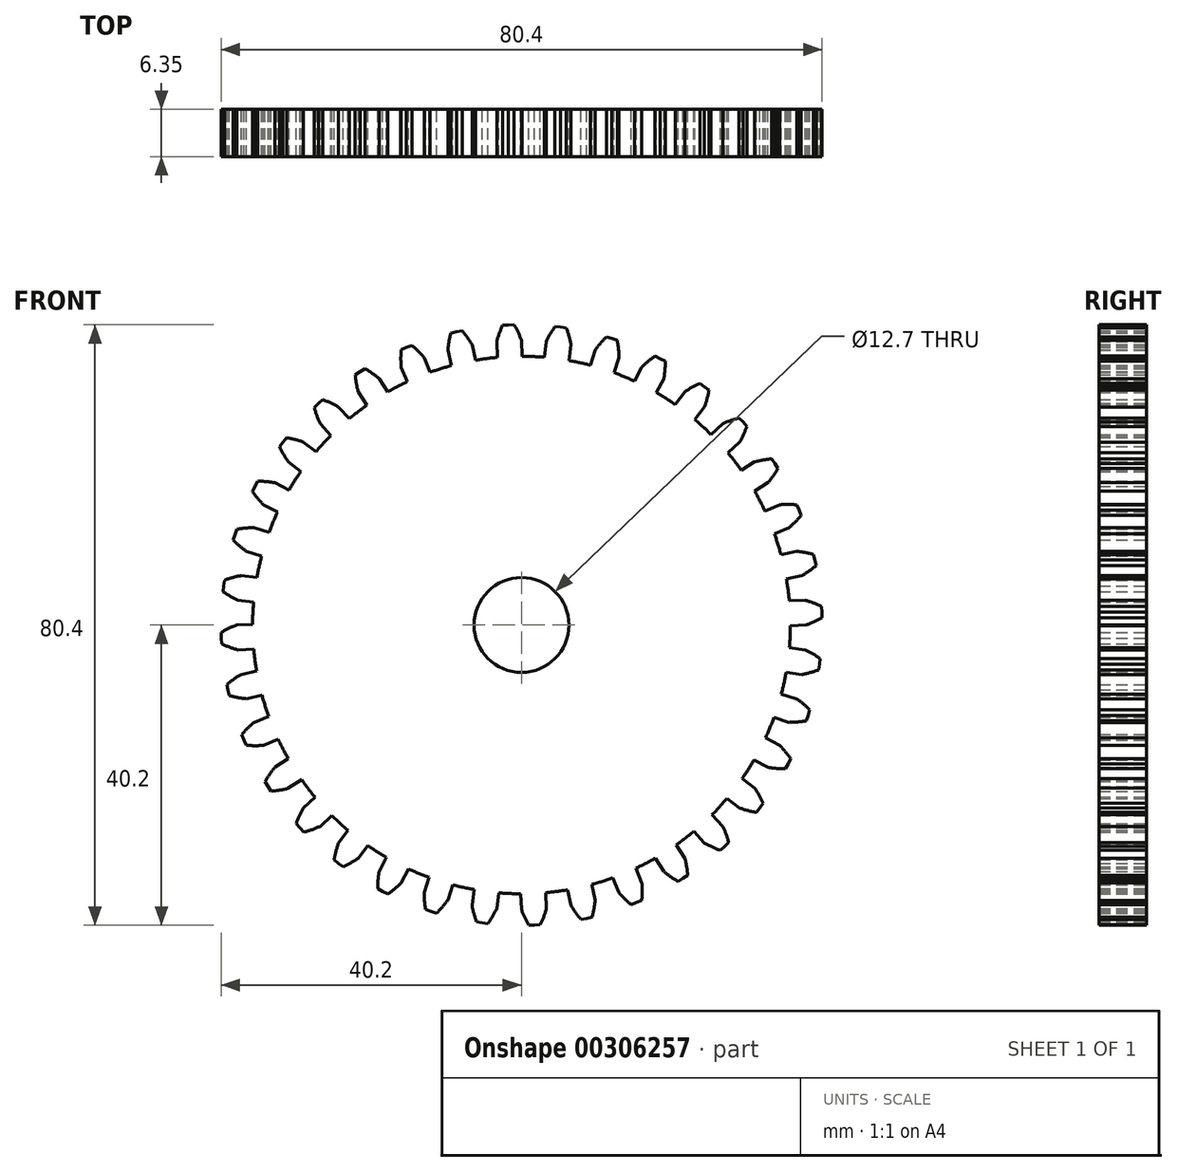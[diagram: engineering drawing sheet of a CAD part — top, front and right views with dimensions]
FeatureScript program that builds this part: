
annotation { "Feature Type Name" : "Feature", "Feature Type Description" : "" }
export const myFeature = defineFeature(function(context is Context, id is Id, definition is map)
    precondition{}
    {
        {
            var Q0;
            Q0=qCreatedBy(makeId("Front.planeOp"),FACE);
            var sketch = newSketch(context, id + "F0", { "sketchPlane" : qUnion([Q0])});
            skArc(sketch, "E0", {"start": v(-3.23, 35.83) * mm, "mid": v(1.57, -35.94) * mm, "end": v(0.1, 35.98) * mm});
            skArc(sketch, "E1.trimOffspring", {"start": v(0, 38.1) * mm, "mid": v(-0.45, 39.17) * mm, "end": v(-0.99, 40.2) * mm});
            skLineSegment(sketch, "E2", {"start": v(0, 38.1) * mm, "end": v(0.1, 35.98) * mm});
            skLineSegment(sketch, "E3", {"start": v(-0.99, 40.2) * mm, "end": v(-1.75, 40.18) * mm});
            skLineSegment(sketch, "E4.MirrorCS", {"start": v(-2.52, 40.13) * mm, "end": v(-1.75, 40.18) * mm});
            skArc(sketch, "E5.MirrorCS", {"start": v(-3.32, 37.95) * mm, "mid": v(-2.97, 39.06) * mm, "end": v(-2.52, 40.13) * mm});
            skLineSegment(sketch, "E6.MirrorCS", {"start": v(-3.32, 37.95) * mm, "end": v(-3.23, 35.83) * mm});
            skPoint(sketch, "E7.orphan", {"position": v(-3.18, 34.7) * mm});
            skPoint(sketch, "E8.orphan", {"position": v(0.14, 34.85) * mm});
            skLineSegment(sketch, "E9.1.0", {"start": v(-31.2, -21.85) * mm, "end": v(-29.42, -20.71) * mm});
            skLineSegment(sketch, "E9.2.0", {"start": v(34.53, -16.1) * mm, "end": v(32.65, -15.12) * mm});
            skLineSegment(sketch, "E10.1.0", {"start": v(-9.86, 36.8) * mm, "end": v(-9.4, 34.73) * mm});
            skArc(sketch, "E10.1.1", {"start": v(-9.86, 36.8) * mm, "mid": v(-9.7, 37.95) * mm, "end": v(-9.45, 39.08) * mm});
            skLineSegment(sketch, "E10.1.2", {"start": v(-9.45, 39.08) * mm, "end": v(-8.7, 39.26) * mm});
            skLineSegment(sketch, "E10.1.3", {"start": v(-7.95, 39.41) * mm, "end": v(-8.7, 39.26) * mm});
            skArc(sketch, "E10.1.4", {"start": v(-6.62, 37.52) * mm, "mid": v(-7.24, 38.5) * mm, "end": v(-7.95, 39.41) * mm});
            skLineSegment(sketch, "E10.1.5", {"start": v(-6.62, 37.52) * mm, "end": v(-6.16, 35.45) * mm});
            skLineSegment(sketch, "E10.2.0", {"start": v(-16.1, 34.53) * mm, "end": v(-15.29, 32.57) * mm});
            skArc(sketch, "E10.2.1", {"start": v(-16.1, 34.53) * mm, "mid": v(-16.15, 35.69) * mm, "end": v(-16.1, 36.85) * mm});
            skLineSegment(sketch, "E10.2.2", {"start": v(-16.1, 36.85) * mm, "end": v(-15.39, 37.15) * mm});
            skLineSegment(sketch, "E10.2.3", {"start": v(-14.68, 37.43) * mm, "end": v(-15.39, 37.15) * mm});
            skArc(sketch, "E10.2.4", {"start": v(-13.03, 35.8) * mm, "mid": v(-13.82, 36.66) * mm, "end": v(-14.68, 37.43) * mm});
            skLineSegment(sketch, "E10.2.5", {"start": v(-13.03, 35.8) * mm, "end": v(-12.22, 33.84) * mm});
            skLineSegment(sketch, "E10.3.0", {"start": v(-21.85, 31.2) * mm, "end": v(-20.71, 29.42) * mm});
            skArc(sketch, "E10.3.1", {"start": v(-21.85, 31.2) * mm, "mid": v(-22.1, 32.34) * mm, "end": v(-22.25, 33.5) * mm});
            skLineSegment(sketch, "E10.3.2", {"start": v(-22.25, 33.5) * mm, "end": v(-21.6, 33.92) * mm});
            skLineSegment(sketch, "E10.3.3", {"start": v(-20.95, 34.32) * mm, "end": v(-21.6, 33.92) * mm});
            skArc(sketch, "E10.3.4", {"start": v(-19.05, 33) * mm, "mid": v(-19.97, 33.7) * mm, "end": v(-20.95, 34.32) * mm});
            skLineSegment(sketch, "E10.3.5", {"start": v(-19.05, 33) * mm, "end": v(-17.9, 31.2) * mm});
            skLineSegment(sketch, "E10.4.0", {"start": v(-26.94, 26.94) * mm, "end": v(-25.5, 25.38) * mm});
            skArc(sketch, "E10.4.1", {"start": v(-26.94, 26.94) * mm, "mid": v(-27.38, 28.01) * mm, "end": v(-27.72, 29.12) * mm});
            skLineSegment(sketch, "E10.4.2", {"start": v(-27.72, 29.12) * mm, "end": v(-27.17, 29.65) * mm});
            skLineSegment(sketch, "E10.4.3", {"start": v(-26.6, 30.16) * mm, "end": v(-27.17, 29.65) * mm});
            skArc(sketch, "E10.4.4", {"start": v(-24.5, 29.19) * mm, "mid": v(-25.52, 29.72) * mm, "end": v(-26.6, 30.16) * mm});
            skLineSegment(sketch, "E10.4.5", {"start": v(-24.5, 29.19) * mm, "end": v(-23.06, 27.62) * mm});
            skLineSegment(sketch, "E10.5.0", {"start": v(-31.2, 21.85) * mm, "end": v(-29.53, 20.56) * mm});
            skArc(sketch, "E10.5.1", {"start": v(-31.2, 21.85) * mm, "mid": v(-31.83, 22.83) * mm, "end": v(-32.36, 23.87) * mm});
            skLineSegment(sketch, "E10.5.2", {"start": v(-32.36, 23.87) * mm, "end": v(-31.9, 24.48) * mm});
            skLineSegment(sketch, "E10.5.3", {"start": v(-31.43, 25.08) * mm, "end": v(-31.9, 24.48) * mm});
            skArc(sketch, "E10.5.4", {"start": v(-29.19, 24.5) * mm, "mid": v(-30.3, 24.84) * mm, "end": v(-31.43, 25.08) * mm});
            skLineSegment(sketch, "E10.5.5", {"start": v(-29.19, 24.5) * mm, "end": v(-27.5, 23.2) * mm});
            skLineSegment(sketch, "E10.6.0", {"start": v(-34.53, 16.1) * mm, "end": v(-32.65, 15.12) * mm});
            skArc(sketch, "E10.6.1", {"start": v(-34.53, 16.1) * mm, "mid": v(-35.31, 16.96) * mm, "end": v(-36.01, 17.88) * mm});
            skLineSegment(sketch, "E10.6.2", {"start": v(-36.01, 17.88) * mm, "end": v(-35.67, 18.57) * mm});
            skLineSegment(sketch, "E10.6.3", {"start": v(-35.3, 19.24) * mm, "end": v(-35.67, 18.57) * mm});
            skArc(sketch, "E10.6.4", {"start": v(-33, 19.05) * mm, "mid": v(-34.15, 19.2) * mm, "end": v(-35.3, 19.24) * mm});
            skLineSegment(sketch, "E10.6.5", {"start": v(-33, 19.05) * mm, "end": v(-31.11, 18.07) * mm});
            skLineSegment(sketch, "E10.7.0", {"start": v(-36.8, 9.86) * mm, "end": v(-34.78, 9.22) * mm});
            skArc(sketch, "E10.7.1", {"start": v(-36.8, 9.86) * mm, "mid": v(-37.72, 10.57) * mm, "end": v(-38.57, 11.36) * mm});
            skLineSegment(sketch, "E10.7.2", {"start": v(-38.57, 11.36) * mm, "end": v(-38.35, 12.1) * mm});
            skLineSegment(sketch, "E10.7.3", {"start": v(-38.1, 12.82) * mm, "end": v(-38.35, 12.1) * mm});
            skArc(sketch, "E10.7.4", {"start": v(-35.8, 13.03) * mm, "mid": v(-36.96, 12.98) * mm, "end": v(-38.1, 12.82) * mm});
            skLineSegment(sketch, "E10.7.5", {"start": v(-35.8, 13.03) * mm, "end": v(-33.78, 12.4) * mm});
            skLineSegment(sketch, "E10.8.0", {"start": v(-37.95, 3.32) * mm, "end": v(-35.85, 3.04) * mm});
            skArc(sketch, "E10.8.1", {"start": v(-37.95, 3.32) * mm, "mid": v(-38.98, 3.86) * mm, "end": v(-39.96, 4.49) * mm});
            skLineSegment(sketch, "E10.8.2", {"start": v(-39.96, 4.49) * mm, "end": v(-39.87, 5.25) * mm});
            skLineSegment(sketch, "E10.8.3", {"start": v(-39.76, 6) * mm, "end": v(-39.87, 5.25) * mm});
            skArc(sketch, "E10.8.4", {"start": v(-37.52, 6.62) * mm, "mid": v(-38.65, 6.36) * mm, "end": v(-39.76, 6) * mm});
            skLineSegment(sketch, "E10.8.5", {"start": v(-37.52, 6.62) * mm, "end": v(-35.42, 6.34) * mm});
            skLineSegment(sketch, "E10.9.0", {"start": v(-37.95, -3.32) * mm, "end": v(-35.83, -3.23) * mm});
            skArc(sketch, "E10.9.1", {"start": v(-37.95, -3.32) * mm, "mid": v(-39.06, -2.97) * mm, "end": v(-40.13, -2.52) * mm});
            skLineSegment(sketch, "E10.9.2", {"start": v(-40.13, -2.52) * mm, "end": v(-40.18, -1.75) * mm});
            skLineSegment(sketch, "E10.9.3", {"start": v(-40.2, -0.99) * mm, "end": v(-40.18, -1.75) * mm});
            skArc(sketch, "E10.9.4", {"start": v(-38.1, 0) * mm, "mid": v(-39.17, -0.45) * mm, "end": v(-40.2, -0.99) * mm});
            skLineSegment(sketch, "E10.9.5", {"start": v(-38.1, 0) * mm, "end": v(-35.98, 0.1) * mm});
            skLineSegment(sketch, "E10.10.0", {"start": v(-36.8, -9.86) * mm, "end": v(-34.73, -9.4) * mm});
            skArc(sketch, "E10.10.1", {"start": v(-36.8, -9.86) * mm, "mid": v(-37.95, -9.7) * mm, "end": v(-39.08, -9.45) * mm});
            skLineSegment(sketch, "E10.10.2", {"start": v(-39.08, -9.45) * mm, "end": v(-39.26, -8.7) * mm});
            skLineSegment(sketch, "E10.10.3", {"start": v(-39.41, -7.95) * mm, "end": v(-39.26, -8.7) * mm});
            skArc(sketch, "E10.10.4", {"start": v(-37.52, -6.62) * mm, "mid": v(-38.5, -7.24) * mm, "end": v(-39.41, -7.95) * mm});
            skLineSegment(sketch, "E10.10.5", {"start": v(-37.52, -6.62) * mm, "end": v(-35.45, -6.16) * mm});
            skLineSegment(sketch, "E10.11.0", {"start": v(-34.53, -16.1) * mm, "end": v(-32.57, -15.29) * mm});
            skArc(sketch, "E10.11.1", {"start": v(-34.53, -16.1) * mm, "mid": v(-35.69, -16.15) * mm, "end": v(-36.85, -16.1) * mm});
            skLineSegment(sketch, "E10.11.2", {"start": v(-36.85, -16.1) * mm, "end": v(-37.15, -15.39) * mm});
            skLineSegment(sketch, "E10.11.3", {"start": v(-37.43, -14.68) * mm, "end": v(-37.15, -15.39) * mm});
            skArc(sketch, "E10.11.4", {"start": v(-35.8, -13.03) * mm, "mid": v(-36.66, -13.82) * mm, "end": v(-37.43, -14.68) * mm});
            skLineSegment(sketch, "E10.11.5", {"start": v(-35.8, -13.03) * mm, "end": v(-33.84, -12.22) * mm});
            skArc(sketch, "E10.12.1", {"start": v(-31.2, -21.85) * mm, "mid": v(-32.34, -22.1) * mm, "end": v(-33.5, -22.25) * mm});
            skLineSegment(sketch, "E10.12.2", {"start": v(-33.5, -22.25) * mm, "end": v(-33.92, -21.6) * mm});
            skLineSegment(sketch, "E10.12.3", {"start": v(-34.32, -20.95) * mm, "end": v(-33.92, -21.6) * mm});
            skArc(sketch, "E10.12.4", {"start": v(-33, -19.05) * mm, "mid": v(-33.7, -19.97) * mm, "end": v(-34.32, -20.95) * mm});
            skLineSegment(sketch, "E10.12.5", {"start": v(-33, -19.05) * mm, "end": v(-31.2, -17.9) * mm});
            skLineSegment(sketch, "E10.13.0", {"start": v(-26.94, -26.94) * mm, "end": v(-25.38, -25.5) * mm});
            skArc(sketch, "E10.13.1", {"start": v(-26.94, -26.94) * mm, "mid": v(-28.01, -27.38) * mm, "end": v(-29.12, -27.72) * mm});
            skLineSegment(sketch, "E10.13.2", {"start": v(-29.12, -27.72) * mm, "end": v(-29.65, -27.17) * mm});
            skLineSegment(sketch, "E10.13.3", {"start": v(-30.16, -26.6) * mm, "end": v(-29.65, -27.17) * mm});
            skArc(sketch, "E10.13.4", {"start": v(-29.19, -24.5) * mm, "mid": v(-29.72, -25.52) * mm, "end": v(-30.16, -26.6) * mm});
            skLineSegment(sketch, "E10.13.5", {"start": v(-29.19, -24.5) * mm, "end": v(-27.62, -23.06) * mm});
            skLineSegment(sketch, "E10.14.0", {"start": v(-21.85, -31.2) * mm, "end": v(-20.56, -29.53) * mm});
            skArc(sketch, "E10.14.1", {"start": v(-21.85, -31.2) * mm, "mid": v(-22.83, -31.83) * mm, "end": v(-23.87, -32.36) * mm});
            skLineSegment(sketch, "E10.14.2", {"start": v(-23.87, -32.36) * mm, "end": v(-24.48, -31.9) * mm});
            skLineSegment(sketch, "E10.14.3", {"start": v(-25.08, -31.43) * mm, "end": v(-24.48, -31.9) * mm});
            skArc(sketch, "E10.14.4", {"start": v(-24.5, -29.19) * mm, "mid": v(-24.84, -30.3) * mm, "end": v(-25.08, -31.43) * mm});
            skLineSegment(sketch, "E10.14.5", {"start": v(-24.5, -29.19) * mm, "end": v(-23.2, -27.5) * mm});
            skLineSegment(sketch, "E10.15.0", {"start": v(-16.1, -34.53) * mm, "end": v(-15.12, -32.65) * mm});
            skArc(sketch, "E10.15.1", {"start": v(-16.1, -34.53) * mm, "mid": v(-16.96, -35.31) * mm, "end": v(-17.88, -36.01) * mm});
            skLineSegment(sketch, "E10.15.2", {"start": v(-17.88, -36.01) * mm, "end": v(-18.57, -35.67) * mm});
            skLineSegment(sketch, "E10.15.3", {"start": v(-19.24, -35.3) * mm, "end": v(-18.57, -35.67) * mm});
            skArc(sketch, "E10.15.4", {"start": v(-19.05, -33) * mm, "mid": v(-19.2, -34.15) * mm, "end": v(-19.24, -35.3) * mm});
            skLineSegment(sketch, "E10.15.5", {"start": v(-19.05, -33) * mm, "end": v(-18.07, -31.11) * mm});
            skLineSegment(sketch, "E10.16.0", {"start": v(-9.86, -36.8) * mm, "end": v(-9.22, -34.78) * mm});
            skArc(sketch, "E10.16.1", {"start": v(-9.86, -36.8) * mm, "mid": v(-10.57, -37.72) * mm, "end": v(-11.36, -38.57) * mm});
            skLineSegment(sketch, "E10.16.2", {"start": v(-11.36, -38.57) * mm, "end": v(-12.1, -38.35) * mm});
            skLineSegment(sketch, "E10.16.3", {"start": v(-12.82, -38.1) * mm, "end": v(-12.1, -38.35) * mm});
            skArc(sketch, "E10.16.4", {"start": v(-13.03, -35.8) * mm, "mid": v(-12.98, -36.96) * mm, "end": v(-12.82, -38.1) * mm});
            skLineSegment(sketch, "E10.16.5", {"start": v(-13.03, -35.8) * mm, "end": v(-12.4, -33.78) * mm});
            skLineSegment(sketch, "E10.17.0", {"start": v(-3.32, -37.95) * mm, "end": v(-3.04, -35.85) * mm});
            skArc(sketch, "E10.17.1", {"start": v(-3.32, -37.95) * mm, "mid": v(-3.86, -38.98) * mm, "end": v(-4.49, -39.96) * mm});
            skLineSegment(sketch, "E10.17.2", {"start": v(-4.49, -39.96) * mm, "end": v(-5.25, -39.87) * mm});
            skLineSegment(sketch, "E10.17.3", {"start": v(-6, -39.76) * mm, "end": v(-5.25, -39.87) * mm});
            skArc(sketch, "E10.17.4", {"start": v(-6.62, -37.52) * mm, "mid": v(-6.36, -38.65) * mm, "end": v(-6, -39.76) * mm});
            skLineSegment(sketch, "E10.17.5", {"start": v(-6.62, -37.52) * mm, "end": v(-6.34, -35.42) * mm});
            skLineSegment(sketch, "E10.18.0", {"start": v(3.32, -37.95) * mm, "end": v(3.23, -35.83) * mm});
            skArc(sketch, "E10.18.1", {"start": v(3.32, -37.95) * mm, "mid": v(2.97, -39.06) * mm, "end": v(2.52, -40.13) * mm});
            skLineSegment(sketch, "E10.18.2", {"start": v(2.52, -40.13) * mm, "end": v(1.75, -40.18) * mm});
            skLineSegment(sketch, "E10.18.3", {"start": v(0.99, -40.2) * mm, "end": v(1.75, -40.18) * mm});
            skArc(sketch, "E10.18.4", {"start": v(0, -38.1) * mm, "mid": v(0.45, -39.17) * mm, "end": v(0.99, -40.2) * mm});
            skLineSegment(sketch, "E10.18.5", {"start": v(0, -38.1) * mm, "end": v(-0.1, -35.98) * mm});
            skLineSegment(sketch, "E10.19.0", {"start": v(9.86, -36.8) * mm, "end": v(9.4, -34.73) * mm});
            skArc(sketch, "E10.19.1", {"start": v(9.86, -36.8) * mm, "mid": v(9.7, -37.95) * mm, "end": v(9.45, -39.08) * mm});
            skLineSegment(sketch, "E10.19.2", {"start": v(9.45, -39.08) * mm, "end": v(8.7, -39.26) * mm});
            skLineSegment(sketch, "E10.19.3", {"start": v(7.95, -39.41) * mm, "end": v(8.7, -39.26) * mm});
            skArc(sketch, "E10.19.4", {"start": v(6.62, -37.52) * mm, "mid": v(7.24, -38.5) * mm, "end": v(7.95, -39.41) * mm});
            skLineSegment(sketch, "E10.19.5", {"start": v(6.62, -37.52) * mm, "end": v(6.16, -35.45) * mm});
            skLineSegment(sketch, "E10.20.0", {"start": v(16.1, -34.53) * mm, "end": v(15.29, -32.57) * mm});
            skArc(sketch, "E10.20.1", {"start": v(16.1, -34.53) * mm, "mid": v(16.15, -35.69) * mm, "end": v(16.1, -36.85) * mm});
            skLineSegment(sketch, "E10.20.2", {"start": v(16.1, -36.85) * mm, "end": v(15.39, -37.15) * mm});
            skLineSegment(sketch, "E10.20.3", {"start": v(14.68, -37.43) * mm, "end": v(15.39, -37.15) * mm});
            skArc(sketch, "E10.20.4", {"start": v(13.03, -35.8) * mm, "mid": v(13.82, -36.66) * mm, "end": v(14.68, -37.43) * mm});
            skLineSegment(sketch, "E10.20.5", {"start": v(13.03, -35.8) * mm, "end": v(12.22, -33.84) * mm});
            skLineSegment(sketch, "E10.21.0", {"start": v(21.85, -31.2) * mm, "end": v(20.71, -29.42) * mm});
            skArc(sketch, "E10.21.1", {"start": v(21.85, -31.2) * mm, "mid": v(22.1, -32.34) * mm, "end": v(22.25, -33.5) * mm});
            skLineSegment(sketch, "E10.21.2", {"start": v(22.25, -33.5) * mm, "end": v(21.6, -33.92) * mm});
            skLineSegment(sketch, "E10.21.3", {"start": v(20.95, -34.32) * mm, "end": v(21.6, -33.92) * mm});
            skArc(sketch, "E10.21.4", {"start": v(19.05, -33) * mm, "mid": v(19.97, -33.7) * mm, "end": v(20.95, -34.32) * mm});
            skLineSegment(sketch, "E10.21.5", {"start": v(19.05, -33) * mm, "end": v(17.9, -31.2) * mm});
            skLineSegment(sketch, "E10.22.0", {"start": v(26.94, -26.94) * mm, "end": v(25.5, -25.38) * mm});
            skArc(sketch, "E10.22.1", {"start": v(26.94, -26.94) * mm, "mid": v(27.38, -28.01) * mm, "end": v(27.72, -29.12) * mm});
            skLineSegment(sketch, "E10.22.2", {"start": v(27.72, -29.12) * mm, "end": v(27.17, -29.65) * mm});
            skLineSegment(sketch, "E10.22.3", {"start": v(26.6, -30.16) * mm, "end": v(27.17, -29.65) * mm});
            skArc(sketch, "E10.22.4", {"start": v(24.5, -29.19) * mm, "mid": v(25.52, -29.72) * mm, "end": v(26.6, -30.16) * mm});
            skLineSegment(sketch, "E10.22.5", {"start": v(24.5, -29.19) * mm, "end": v(23.06, -27.62) * mm});
            skLineSegment(sketch, "E10.23.0", {"start": v(31.2, -21.85) * mm, "end": v(29.53, -20.56) * mm});
            skArc(sketch, "E10.23.1", {"start": v(31.2, -21.85) * mm, "mid": v(31.83, -22.83) * mm, "end": v(32.36, -23.87) * mm});
            skLineSegment(sketch, "E10.23.2", {"start": v(32.36, -23.87) * mm, "end": v(31.9, -24.48) * mm});
            skLineSegment(sketch, "E10.23.3", {"start": v(31.43, -25.08) * mm, "end": v(31.9, -24.48) * mm});
            skArc(sketch, "E10.23.4", {"start": v(29.19, -24.5) * mm, "mid": v(30.3, -24.84) * mm, "end": v(31.43, -25.08) * mm});
            skLineSegment(sketch, "E10.23.5", {"start": v(29.19, -24.5) * mm, "end": v(27.5, -23.2) * mm});
            skArc(sketch, "E10.24.1", {"start": v(34.53, -16.1) * mm, "mid": v(35.31, -16.96) * mm, "end": v(36.01, -17.88) * mm});
            skLineSegment(sketch, "E10.24.2", {"start": v(36.01, -17.88) * mm, "end": v(35.67, -18.57) * mm});
            skLineSegment(sketch, "E10.24.3", {"start": v(35.3, -19.24) * mm, "end": v(35.67, -18.57) * mm});
            skArc(sketch, "E10.24.4", {"start": v(33, -19.05) * mm, "mid": v(34.15, -19.2) * mm, "end": v(35.3, -19.24) * mm});
            skLineSegment(sketch, "E10.24.5", {"start": v(33, -19.05) * mm, "end": v(31.11, -18.07) * mm});
            skLineSegment(sketch, "E10.25.0", {"start": v(36.8, -9.86) * mm, "end": v(34.78, -9.22) * mm});
            skArc(sketch, "E10.25.1", {"start": v(36.8, -9.86) * mm, "mid": v(37.72, -10.57) * mm, "end": v(38.57, -11.36) * mm});
            skLineSegment(sketch, "E10.25.2", {"start": v(38.57, -11.36) * mm, "end": v(38.35, -12.1) * mm});
            skLineSegment(sketch, "E10.25.3", {"start": v(38.1, -12.82) * mm, "end": v(38.35, -12.1) * mm});
            skArc(sketch, "E10.25.4", {"start": v(35.8, -13.03) * mm, "mid": v(36.96, -12.98) * mm, "end": v(38.1, -12.82) * mm});
            skLineSegment(sketch, "E10.25.5", {"start": v(35.8, -13.03) * mm, "end": v(33.78, -12.4) * mm});
            skLineSegment(sketch, "E10.26.0", {"start": v(37.95, -3.32) * mm, "end": v(35.85, -3.04) * mm});
            skArc(sketch, "E10.26.1", {"start": v(37.95, -3.32) * mm, "mid": v(38.98, -3.86) * mm, "end": v(39.96, -4.49) * mm});
            skLineSegment(sketch, "E10.26.2", {"start": v(39.96, -4.49) * mm, "end": v(39.87, -5.25) * mm});
            skLineSegment(sketch, "E10.26.3", {"start": v(39.76, -6) * mm, "end": v(39.87, -5.25) * mm});
            skArc(sketch, "E10.26.4", {"start": v(37.52, -6.62) * mm, "mid": v(38.65, -6.36) * mm, "end": v(39.76, -6) * mm});
            skLineSegment(sketch, "E10.26.5", {"start": v(37.52, -6.62) * mm, "end": v(35.42, -6.34) * mm});
            skLineSegment(sketch, "E10.27.0", {"start": v(37.95, 3.32) * mm, "end": v(35.83, 3.23) * mm});
            skArc(sketch, "E10.27.1", {"start": v(37.95, 3.32) * mm, "mid": v(39.06, 2.97) * mm, "end": v(40.13, 2.52) * mm});
            skLineSegment(sketch, "E10.27.2", {"start": v(40.13, 2.52) * mm, "end": v(40.18, 1.75) * mm});
            skLineSegment(sketch, "E10.27.3", {"start": v(40.2, 0.99) * mm, "end": v(40.18, 1.75) * mm});
            skArc(sketch, "E10.27.4", {"start": v(38.1, 0) * mm, "mid": v(39.17, 0.45) * mm, "end": v(40.2, 0.99) * mm});
            skLineSegment(sketch, "E10.27.5", {"start": v(38.1, 0) * mm, "end": v(35.98, -0.1) * mm});
            skLineSegment(sketch, "E10.28.0", {"start": v(36.8, 9.86) * mm, "end": v(34.73, 9.4) * mm});
            skArc(sketch, "E10.28.1", {"start": v(36.8, 9.86) * mm, "mid": v(37.95, 9.7) * mm, "end": v(39.08, 9.45) * mm});
            skLineSegment(sketch, "E10.28.2", {"start": v(39.08, 9.45) * mm, "end": v(39.26, 8.7) * mm});
            skLineSegment(sketch, "E10.28.3", {"start": v(39.41, 7.95) * mm, "end": v(39.26, 8.7) * mm});
            skArc(sketch, "E10.28.4", {"start": v(37.52, 6.62) * mm, "mid": v(38.5, 7.24) * mm, "end": v(39.41, 7.95) * mm});
            skLineSegment(sketch, "E10.28.5", {"start": v(37.52, 6.62) * mm, "end": v(35.45, 6.16) * mm});
            skLineSegment(sketch, "E10.29.0", {"start": v(34.53, 16.1) * mm, "end": v(32.57, 15.29) * mm});
            skArc(sketch, "E10.29.1", {"start": v(34.53, 16.1) * mm, "mid": v(35.69, 16.15) * mm, "end": v(36.85, 16.1) * mm});
            skLineSegment(sketch, "E10.29.2", {"start": v(36.85, 16.1) * mm, "end": v(37.15, 15.39) * mm});
            skLineSegment(sketch, "E10.29.3", {"start": v(37.43, 14.68) * mm, "end": v(37.15, 15.39) * mm});
            skArc(sketch, "E10.29.4", {"start": v(35.8, 13.03) * mm, "mid": v(36.66, 13.82) * mm, "end": v(37.43, 14.68) * mm});
            skLineSegment(sketch, "E10.29.5", {"start": v(35.8, 13.03) * mm, "end": v(33.84, 12.22) * mm});
            skLineSegment(sketch, "E10.30.0", {"start": v(31.2, 21.85) * mm, "end": v(29.42, 20.71) * mm});
            skArc(sketch, "E10.30.1", {"start": v(31.2, 21.85) * mm, "mid": v(32.34, 22.1) * mm, "end": v(33.5, 22.25) * mm});
            skLineSegment(sketch, "E10.30.2", {"start": v(33.5, 22.25) * mm, "end": v(33.92, 21.6) * mm});
            skLineSegment(sketch, "E10.30.3", {"start": v(34.32, 20.95) * mm, "end": v(33.92, 21.6) * mm});
            skArc(sketch, "E10.30.4", {"start": v(33, 19.05) * mm, "mid": v(33.7, 19.97) * mm, "end": v(34.32, 20.95) * mm});
            skLineSegment(sketch, "E10.30.5", {"start": v(33, 19.05) * mm, "end": v(31.2, 17.9) * mm});
            skLineSegment(sketch, "E10.31.0", {"start": v(26.94, 26.94) * mm, "end": v(25.38, 25.5) * mm});
            skArc(sketch, "E10.31.1", {"start": v(26.94, 26.94) * mm, "mid": v(28.01, 27.38) * mm, "end": v(29.12, 27.72) * mm});
            skLineSegment(sketch, "E10.31.2", {"start": v(29.12, 27.72) * mm, "end": v(29.65, 27.17) * mm});
            skLineSegment(sketch, "E10.31.3", {"start": v(30.16, 26.6) * mm, "end": v(29.65, 27.17) * mm});
            skArc(sketch, "E10.31.4", {"start": v(29.19, 24.5) * mm, "mid": v(29.72, 25.52) * mm, "end": v(30.16, 26.6) * mm});
            skLineSegment(sketch, "E10.31.5", {"start": v(29.19, 24.5) * mm, "end": v(27.62, 23.06) * mm});
            skLineSegment(sketch, "E10.32.0", {"start": v(21.85, 31.2) * mm, "end": v(20.56, 29.53) * mm});
            skArc(sketch, "E10.32.1", {"start": v(21.85, 31.2) * mm, "mid": v(22.83, 31.83) * mm, "end": v(23.87, 32.36) * mm});
            skLineSegment(sketch, "E10.32.2", {"start": v(23.87, 32.36) * mm, "end": v(24.48, 31.9) * mm});
            skLineSegment(sketch, "E10.32.3", {"start": v(25.08, 31.43) * mm, "end": v(24.48, 31.9) * mm});
            skArc(sketch, "E10.32.4", {"start": v(24.5, 29.19) * mm, "mid": v(24.84, 30.3) * mm, "end": v(25.08, 31.43) * mm});
            skLineSegment(sketch, "E10.32.5", {"start": v(24.5, 29.19) * mm, "end": v(23.2, 27.5) * mm});
            skLineSegment(sketch, "E10.33.0", {"start": v(16.1, 34.53) * mm, "end": v(15.12, 32.65) * mm});
            skArc(sketch, "E10.33.1", {"start": v(16.1, 34.53) * mm, "mid": v(16.96, 35.31) * mm, "end": v(17.88, 36.01) * mm});
            skLineSegment(sketch, "E10.33.2", {"start": v(17.88, 36.01) * mm, "end": v(18.57, 35.67) * mm});
            skLineSegment(sketch, "E10.33.3", {"start": v(19.24, 35.3) * mm, "end": v(18.57, 35.67) * mm});
            skArc(sketch, "E10.33.4", {"start": v(19.05, 33) * mm, "mid": v(19.2, 34.15) * mm, "end": v(19.24, 35.3) * mm});
            skLineSegment(sketch, "E10.33.5", {"start": v(19.05, 33) * mm, "end": v(18.07, 31.11) * mm});
            skLineSegment(sketch, "E10.34.0", {"start": v(9.86, 36.8) * mm, "end": v(9.22, 34.78) * mm});
            skArc(sketch, "E10.34.1", {"start": v(9.86, 36.8) * mm, "mid": v(10.57, 37.72) * mm, "end": v(11.36, 38.57) * mm});
            skLineSegment(sketch, "E10.34.2", {"start": v(11.36, 38.57) * mm, "end": v(12.1, 38.35) * mm});
            skLineSegment(sketch, "E10.34.3", {"start": v(12.82, 38.1) * mm, "end": v(12.1, 38.35) * mm});
            skArc(sketch, "E10.34.4", {"start": v(13.03, 35.8) * mm, "mid": v(12.98, 36.96) * mm, "end": v(12.82, 38.1) * mm});
            skLineSegment(sketch, "E10.34.5", {"start": v(13.03, 35.8) * mm, "end": v(12.4, 33.78) * mm});
            skLineSegment(sketch, "E10.35.0", {"start": v(3.32, 37.95) * mm, "end": v(3.04, 35.85) * mm});
            skArc(sketch, "E10.35.1", {"start": v(3.32, 37.95) * mm, "mid": v(3.86, 38.98) * mm, "end": v(4.49, 39.96) * mm});
            skLineSegment(sketch, "E10.35.2", {"start": v(4.49, 39.96) * mm, "end": v(5.25, 39.87) * mm});
            skLineSegment(sketch, "E10.35.3", {"start": v(6, 39.76) * mm, "end": v(5.25, 39.87) * mm});
            skArc(sketch, "E10.35.4", {"start": v(6.62, 37.52) * mm, "mid": v(6.36, 38.65) * mm, "end": v(6, 39.76) * mm});
            skLineSegment(sketch, "E10.35.5", {"start": v(6.62, 37.52) * mm, "end": v(6.34, 35.42) * mm});
            skCircle(sketch, "E11", {"center": v(0, 0) * mm, "radius": 6.35 * mm});
            skSolve(sketch);
        }
        {
            var Q0;
            Q0 = qSketchRegion(id + "F0", true);
            extrude(context, id + "F1", {"entities" : qUnion([Q0]), "depth" : 6.35 * mm});
        }
    });
